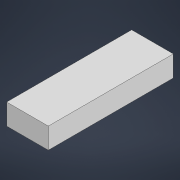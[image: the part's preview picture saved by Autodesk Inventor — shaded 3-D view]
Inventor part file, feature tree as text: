
AUTODESK INVENTOR PART (.ipt)
format: ipt  version: 2022 (Build 260153070, 153G)  size: 85,504 bytes
history: native  units: mm
features: other x1, extrude x1, sketch x1
ambient origin geometry x8: Origin, YZ Plane, XZ Plane, XY Plane, X Axis, Y Axis, Z Axis, Center Point
bodies: Body1 (feature_tree)
feature tree (3):
  other  "Твердое тело1"
  extrude  "Выдавливание1"  Depth=20.0mm
  sketch  "Эскиз1"
